# Revit family: Furniture-Workstation-Midmark-Care_Exchange-6283-Wall1
name_source: partatom
category: Furniture
revit_build: Autodesk Revit 2016 (Build: 20170117_1200(x64)
units: mm (PartAtom-declared; Revit-internal decimal feet)

## family parameters
Cut with Voids When Loaded = No
Host = Face
OmniClass Number = 23.40.70.11.14.11
OmniClass Title = Medical Equipment
Room Calculation Point = No
Shared = No

## types (2) — shared parameters
Assembly Code = E1020810
Default Elevation = 4' - 0"
Description = Heavy Duty Wall Mounted Workstation
Manufacturer = Midmark
Material = Paint-Midmark-Mist
Model = 6283
Product Documentation Link = http://www.midmark.com
Product Name = MIDMARK 6283-CARE EXCHANGE® WORKSTATION
Product Page URL = http://www.midmark.com
Type Comments = This heavy duty wall mounted workstation is designed with an increased weight capacity and independent height adjustment for all-in-one PC based technology components.
URL = www.midmark.com

## per-type parameters (varying)
| type | Monitor Arm Depth From Center | Monitor Arm Height From Center | Monitor Arm Width From Center | Platform Depth From Wall | Platform Height From Center | Platform Width From Center | Show Extension Arm | Show Standard Arm |
| 6283 | 2' - 0 27/32" | 0' - 8 15/32" | 0' - 0" | 2' - 0" | 0' - 11 1/32" | 0' - 0" | No | Yes |
| 6283 - Extension Arm | 2' - 8 9/16" | 0' - 4 9/32" | 0' - 1 1/8" | 2' - 8" | 0' - 7 1/32" | 0' - 1 1/8" | Yes | No |

## geometry (parser evidence)
native form markers: Blend x4, Sweep x36
no freeform markers — native parametric forms only
